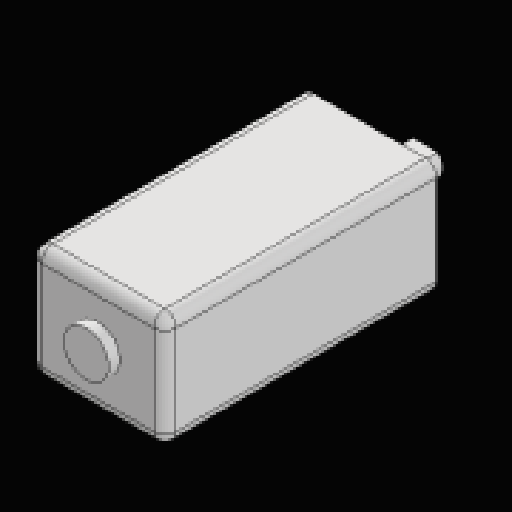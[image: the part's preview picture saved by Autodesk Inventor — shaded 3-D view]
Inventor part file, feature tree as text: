
AUTODESK INVENTOR PART (.ipt)
format: ipt  version: 2023.2 (Build 272271030, 271C)  size: 152,064 bytes
history: native  units: mm
features: sketch x5, extrude x4, fillet x1, hole x1, projected_geometry x1
ambient origin geometry x8: Origin, YZ Plane, XZ Plane, XY Plane, X Axis, Y Axis, Z Axis, Center Point
bodies: Solid1 (feature_tree)
feature tree (12):
  extrude  "Extrusion1"  Depth=10.0mm
  extrude  "Extrusion2"  Depth=4.0mm
  extrude  "Extrusion3"  Depth=4.0mm
  extrude  "Extrusion4"  Depth=1.0mm
  fillet  "Fillet1"  Radius=2.5mm
  hole  "Hole1"  [1 undecoded]
  sketch  "Sketch1"  dims[d0=12.0mm d1=10.0mm]
  sketch  "Sketch2"  dims[d2=24.25mm d3=0.0mm d4=4.0mm]
  sketch  "Sketch3"  dims[d5=1.0mm d6=0.0mm d7=4.0mm]
  sketch  "Sketch4"  dims[d8=1.0mm d9=0.0mm d10=3.0mm d11=2.5mm]
  sketch  "Sketch5"  dims[d12=4.0mm d13=0.0mm d14=1.0mm d15=4.5mm d16=4.5mm d17=1.221mm d18=1.0mm d19=4.0mm d20=2.0mm d21=90.0deg d22=1.0mm d23=0.0mm]
  projected_geometry  "Projected Loop1"
note: 1 required parameter value undecoded (feature->parameter linkage not recoverable at this tier; creation-order binding heuristic only, values carry confidence <= 0.55)
